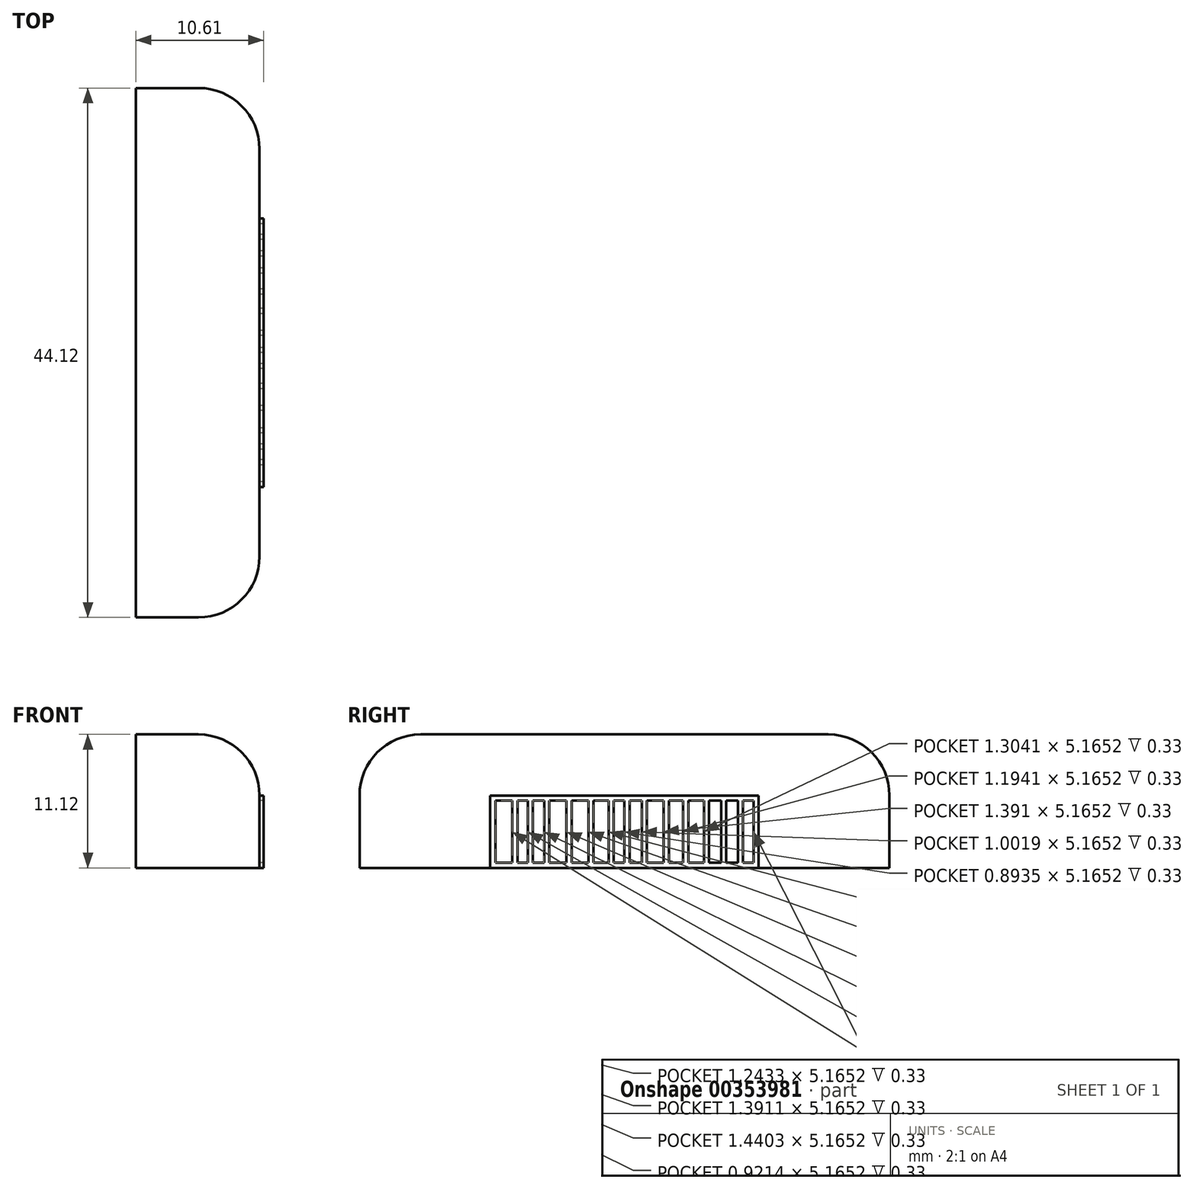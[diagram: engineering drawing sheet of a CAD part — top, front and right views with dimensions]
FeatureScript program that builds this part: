
annotation { "Feature Type Name" : "Feature", "Feature Type Description" : "" }
export const myFeature = defineFeature(function(context is Context, id is Id, definition is map)
    precondition{}
    {
        {
            var Q0;
            Q0=qCreatedBy(makeId("Right.planeOp"),FACE);
            var sketch = newSketch(context, id + "F0", { "sketchPlane" : qUnion([Q0])});
            skPoint(sketch, "E0.middle", {"position": v(0, 0) * mm});
            skLineSegment(sketch, "E1.bottom", {"start": v(22.06, -5.56) * mm, "end": v(-22.06, -5.56) * mm});
            skLineSegment(sketch, "E1.top", {"start": v(22.06, 5.56) * mm, "end": v(-22.06, 5.56) * mm});
            skLineSegment(sketch, "E1.left", {"start": v(22.06, -5.56) * mm, "end": v(22.06, 5.56) * mm});
            skLineSegment(sketch, "E1.right", {"start": v(-22.06, -5.56) * mm, "end": v(-22.06, 5.56) * mm});
            skSolve(sketch);
        }
        {
            var Q0;
            {var subQ0=sQuery(id+"F0.wireOp",EDGE,"QhqdrkBK-WLEr-STOJ-mHX4-kAFYpGoHdUyc");Q0=makeQuery(id+"F0.imprint","IMPRINT",FACE,{"disambiguationData":[TD([[makeQuery(id+"F0.imprint","IMPRINT",EDGE,{"derivedFrom":subQ0}),-1.0]])]});}
            var Q1;
            {var subQ0=sQuery(id+"F0.wireOp",EDGE,"E1.left");Q1=makeQuery(id+"F0.imprint","IMPRINT",FACE,{"disambiguationData":[TD([[makeQuery(id+"F0.imprint","IMPRINT",EDGE,{"derivedFrom":subQ0}),1.0]])]});}
            var Q2;
            {var subQ0=sQuery(id+"F0.wireOp",EDGE,"KxqXMrYp-0MTx-9sh7-7Cav-ISwPpvUKqUXm");Q2=makeQuery(id+"F0.imprint","IMPRINT",FACE,{"disambiguationData":[TD([[makeQuery(id+"F0.imprint","IMPRINT",EDGE,{"derivedFrom":subQ0}),-1.0]])]});}
            var Q3;
            {var subQ0=sQuery(id+"F0.wireOp",EDGE,"E1.right");Q3=makeQuery(id+"F0.imprint","IMPRINT",FACE,{"disambiguationData":[TD([[makeQuery(id+"F0.imprint","IMPRINT",EDGE,{"derivedFrom":subQ0}),-1.0]])]});}
            var Q4;
            {var subQ0=sQuery(id+"F0.wireOp",EDGE,"ox9cvODF-zMUq-gVxx-R5c6-Xg9GAgzpbPEs.left");Q4=makeQuery(id+"F0.imprint","IMPRINT",FACE,{"disambiguationData":[TD([[makeQuery(id+"F0.imprint","IMPRINT",EDGE,{"derivedFrom":subQ0}),1.0]])]});}
            var Q5;
            {var subQ0=sQuery(id+"F0.wireOp",EDGE,"E5YEkzb1-qd7j-ADr4-wAvl-YFfucIowREs1");Q5=makeQuery(id+"F0.imprint","IMPRINT",FACE,{"disambiguationData":[TD([[makeQuery(id+"F0.imprint","IMPRINT",EDGE,{"derivedFrom":subQ0}),-1.0]])]});}
            var Q6;
            {var subQ0=sQuery(id+"F0.wireOp",EDGE,"7jatnHy1-lAWK-yFio-aBgb-gTgx4ws20swl");Q6=makeQuery(id+"F0.imprint","IMPRINT",FACE,{"disambiguationData":[TD([[makeQuery(id+"F0.imprint","IMPRINT",EDGE,{"derivedFrom":subQ0}),1.0]])]});}
            var Q7;
            {var subQ0=sQuery(id+"F0.wireOp",EDGE,"5BvGlgIY-R3Sq-EqC4-0kwV-YxnTdAeXIUOZ");Q7=makeQuery(id+"F0.imprint","IMPRINT",FACE,{"disambiguationData":[TD([[makeQuery(id+"F0.imprint","IMPRINT",EDGE,{"derivedFrom":subQ0}),1.0]])]});}
            var Q8;
            {var subQ0=sQuery(id+"F0.wireOp",EDGE,"ox9cvODF-zMUq-gVxx-R5c6-Xg9GAgzpbPEs.right");Q8=makeQuery(id+"F0.imprint","IMPRINT",FACE,{"disambiguationData":[TD([[makeQuery(id+"F0.imprint","IMPRINT",EDGE,{"derivedFrom":subQ0}),-1.0]])]});}
            var Q9;
            {var subQ0=sQuery(id+"F0.wireOp",EDGE,"a5BHEEzq-IyKY-KC0P-sr2h-TXtUwZTsSAfV");Q9=makeQuery(id+"F0.imprint","IMPRINT",FACE,{"disambiguationData":[TD([[makeQuery(id+"F0.imprint","IMPRINT",EDGE,{"derivedFrom":subQ0}),1.0]])]});}
            var Q10;
            {var subQ0=sQuery(id+"F0.wireOp",EDGE,"bVTurAre-xmbO-HN2j-k0kJ-VzDN6Xv9tE0l");Q10=makeQuery(id+"F0.imprint","IMPRINT",FACE,{"disambiguationData":[TD([[makeQuery(id+"F0.imprint","IMPRINT",EDGE,{"derivedFrom":subQ0}),1.0]])]});}
            var Q11;
            {var subQ0=sQuery(id+"F0.wireOp",EDGE,"8v8lMbt2-ct1U-efL5-hqXj-f8Gs2E29IiBH");Q11=makeQuery(id+"F0.imprint","IMPRINT",FACE,{"disambiguationData":[TD([[makeQuery(id+"F0.imprint","IMPRINT",EDGE,{"derivedFrom":subQ0}),1.0]])]});}
            var Q12;
            {var subQ0=sQuery(id+"F0.wireOp",EDGE,"JvaCiwvk-U77r-NFcJ-Rx3I-SeJYftzx37q4");Q12=makeQuery(id+"F0.imprint","IMPRINT",FACE,{"disambiguationData":[TD([[makeQuery(id+"F0.imprint","IMPRINT",EDGE,{"derivedFrom":subQ0}),-1.0]])]});}
            extrude(context, id + "F1", {"entities" : qUnion([Q0, Q1, Q2, Q3, Q4, Q5, Q6, Q7, Q8, Q9, Q10, Q11, Q12]), "endBound" : BoundingType.SYMMETRIC, "depth" : 10.28 * mm});
        }
        {
            var Q0;
            Q0=makeQuery(id+"F1.opExtrude","CAP_EDGE",EDGE,{"disambiguationData":[OSD([sQuery(id+"F0.wireOp",EDGE,"E1.left")])],"isStart":false});
            var Q1;
            Q1=makeQuery(id+"F1.opExtrude","CAP_EDGE",EDGE,{"disambiguationData":[OSD([sQuery(id+"F0.wireOp",EDGE,"E1.right")])],"isStart":false});
            fillet(context, id + "F2", {"entities" : qUnion([Q0, Q1]), "radius" : 5.08 * mm, "tangentPropagation" : true, "allowEdgeOverflow" : false});
        }
        {
            var Q0;
            Q0=makeQuery(id+"F1.opExtrude","SWEPT_EDGE",EDGE,{"disambiguationData":[OSD([sQuery(id+"F0.wireOp",EDGE,"E1.top"),sQuery(id+"F0.wireOp",EDGE,"E1.left")])]});
            fillet(context, id + "F3", {"entities" : qUnion([Q0]), "radius" : 5.08 * mm, "tangentPropagation" : true, "allowEdgeOverflow" : false});
        }
        {
            var Q0;
            Q0=makeQuery(id+"F1.opExtrude","CAP_FACE",FACE,{"disambiguationData":[OSD([sQuery(id+"F0.wireOp",EDGE,"E1.bottom"),sQuery(id+"F0.wireOp",EDGE,"E1.top"),sQuery(id+"F0.wireOp",EDGE,"E1.left"),sQuery(id+"F0.wireOp",EDGE,"E1.right")])],"isStart":false});
            var sketch = newSketch(context, id + "F4", { "sketchPlane" : qUnion([Q0])});
            skLineSegment(sketch, "E2.bottom", {"start": v(11.18, -5.56) * mm, "end": v(-11.18, -5.56) * mm});
            skLineSegment(sketch, "E2.top", {"start": v(11.18, 0.47) * mm, "end": v(-11.18, 0.47) * mm});
            skLineSegment(sketch, "E2.left", {"start": v(11.18, -5.56) * mm, "end": v(11.18, 0.47) * mm});
            skLineSegment(sketch, "E2.right", {"start": v(-11.18, -5.56) * mm, "end": v(-11.18, 0.47) * mm});
            skPoint(sketch, "E2.middle", {"position": v(0, -2.54) * mm});
            skLineSegment(sketch, "E3", {"start": v(-8.91, 0.04) * mm, "end": v(-8.91, -5.13) * mm});
            skLineSegment(sketch, "E4", {"start": v(-8.91, -5.56) * mm, "end": v(-6.7, -5.56) * mm});
            skLineSegment(sketch, "E5", {"start": v(-6.7, -5.13) * mm, "end": v(-6.7, 0.04) * mm});
            skLineSegment(sketch, "E6", {"start": v(-6.7, 0.47) * mm, "end": v(-4.82, 0.47) * mm});
            skLineSegment(sketch, "E7", {"start": v(-4.82, 0.04) * mm, "end": v(-4.82, -5.13) * mm});
            skLineSegment(sketch, "E8", {"start": v(-4.82, -5.56) * mm, "end": v(-3, -5.56) * mm});
            skLineSegment(sketch, "E9", {"start": v(-3, -5.13) * mm, "end": v(-3, 0.04) * mm});
            skLineSegment(sketch, "E10", {"start": v(-3, 0.47) * mm, "end": v(-1.33, 0.47) * mm});
            skLineSegment(sketch, "E11", {"start": v(-1.33, 0.04) * mm, "end": v(-1.33, -5.13) * mm});
            skLineSegment(sketch, "E12", {"start": v(-1.33, -5.56) * mm, "end": v(0, -5.56) * mm});
            skLineSegment(sketch, "E13", {"start": v(0, -5.13) * mm, "end": v(0, 0.04) * mm});
            skLineSegment(sketch, "E14", {"start": v(0, 0.47) * mm, "end": v(1.43, 0.47) * mm});
            skLineSegment(sketch, "E15", {"start": v(1.43, 0.04) * mm, "end": v(1.43, -5.13) * mm});
            skLineSegment(sketch, "E16", {"start": v(1.43, -5.56) * mm, "end": v(3.26, -5.56) * mm});
            skLineSegment(sketch, "E17", {"start": v(3.26, -5.13) * mm, "end": v(3.26, 0.04) * mm});
            skLineSegment(sketch, "E18", {"start": v(3.26, 0.47) * mm, "end": v(4.88, 0.47) * mm});
            skLineSegment(sketch, "E19", {"start": v(4.88, 0.04) * mm, "end": v(4.88, -5.13) * mm});
            skLineSegment(sketch, "E20", {"start": v(4.88, -5.56) * mm, "end": v(7.05, -5.56) * mm});
            skLineSegment(sketch, "E21", {"start": v(7.05, -5.13) * mm, "end": v(7.05, 0.04) * mm});
            skLineSegment(sketch, "E22", {"start": v(7.05, 0.47) * mm, "end": v(8.48, 0.47) * mm});
            skLineSegment(sketch, "E23", {"start": v(8.48, 0.04) * mm, "end": v(8.48, -5.13) * mm});
            skLineSegment(sketch, "E24", {"start": v(8.48, -5.56) * mm, "end": v(9.44, -5.56) * mm});
            skLineSegment(sketch, "E25", {"start": v(9.44, -5.13) * mm, "end": v(9.44, 0.04) * mm});
            skLineSegment(sketch, "E26.0", {"start": v(10.75, 0.04) * mm, "end": v(9.87, 0.04) * mm});
            skLineSegment(sketch, "E27.0", {"start": v(-10.75, -5.13) * mm, "end": v(-10.75, 0.04) * mm});
            skLineSegment(sketch, "E28.0", {"start": v(10.75, -5.13) * mm, "end": v(10.75, 0.04) * mm});
            skLineSegment(sketch, "E29.0", {"start": v(10.75, -5.13) * mm, "end": v(9.87, -5.13) * mm});
            skLineSegment(sketch, "E30.0", {"start": v(-9.34, 0.04) * mm, "end": v(-9.34, -5.13) * mm});
            skLineSegment(sketch, "E31.0", {"start": v(-6.26, -5.13) * mm, "end": v(-6.26, 0.04) * mm});
            skLineSegment(sketch, "E32.0", {"start": v(-4.4, 0.04) * mm, "end": v(-4.4, -5.13) * mm});
            skLineSegment(sketch, "E33.0", {"start": v(-2.57, -5.13) * mm, "end": v(-2.57, 0.04) * mm});
            skLineSegment(sketch, "E34.0", {"start": v(-0.9, 0.04) * mm, "end": v(-0.9, -5.13) * mm});
            skLineSegment(sketch, "E35.0", {"start": v(0.43, -5.13) * mm, "end": v(0.43, 0.04) * mm});
            skLineSegment(sketch, "E36.0", {"start": v(1.87, 0.04) * mm, "end": v(1.87, -5.13) * mm});
            skLineSegment(sketch, "E37.0", {"start": v(3.69, -5.13) * mm, "end": v(3.69, 0.04) * mm});
            skLineSegment(sketch, "E38.0", {"start": v(5.31, 0.04) * mm, "end": v(5.31, -5.13) * mm});
            skLineSegment(sketch, "E39.0", {"start": v(6.62, -5.13) * mm, "end": v(6.62, 0.04) * mm});
            skLineSegment(sketch, "E40.0", {"start": v(8.05, 0.04) * mm, "end": v(8.05, -5.13) * mm});
            skLineSegment(sketch, "E41.0", {"start": v(9.87, -5.13) * mm, "end": v(9.87, 0.04) * mm});
            skLineSegment(sketch, "E42", {"start": v(-8.05, 0.04) * mm, "end": v(-8.05, -5.13) * mm});
            skLineSegment(sketch, "E43.0", {"start": v(-7.62, 0.04) * mm, "end": v(-7.62, -5.13) * mm});
            skLineSegment(sketch, "E44.trimOffspring", {"start": v(0, -5.13) * mm, "end": v(-0.9, -5.13) * mm});
            skLineSegment(sketch, "E45.trimOffspring", {"start": v(1.43, -5.13) * mm, "end": v(0.43, -5.13) * mm});
            skLineSegment(sketch, "E46.trimOffspring", {"start": v(-1.33, -5.13) * mm, "end": v(-2.57, -5.13) * mm});
            skLineSegment(sketch, "E47.trimOffspring", {"start": v(-3, -5.13) * mm, "end": v(-4.4, -5.13) * mm});
            skLineSegment(sketch, "E48.trimOffspring", {"start": v(3.26, -5.13) * mm, "end": v(1.87, -5.13) * mm});
            skLineSegment(sketch, "E49.trimOffspring", {"start": v(4.88, -5.13) * mm, "end": v(3.69, -5.13) * mm});
            skLineSegment(sketch, "E50.trimOffspring", {"start": v(6.62, -5.13) * mm, "end": v(5.31, -5.13) * mm});
            skLineSegment(sketch, "E51.trimOffspring", {"start": v(8.05, -5.13) * mm, "end": v(7.05, -5.13) * mm});
            skLineSegment(sketch, "E52.trimOffspring", {"start": v(9.44, -5.13) * mm, "end": v(8.48, -5.13) * mm});
            skLineSegment(sketch, "E53.trimOffspring", {"start": v(-4.82, -5.13) * mm, "end": v(-6.26, -5.13) * mm});
            skLineSegment(sketch, "E54.trimOffspring", {"start": v(-6.7, -5.13) * mm, "end": v(-7.62, -5.13) * mm});
            skLineSegment(sketch, "E55.trimOffspring", {"start": v(-8.05, -5.13) * mm, "end": v(-8.91, -5.13) * mm});
            skLineSegment(sketch, "E56.trimOffspring", {"start": v(-9.34, -5.13) * mm, "end": v(-10.75, -5.13) * mm});
            skLineSegment(sketch, "E57.trimOffspring", {"start": v(-9.34, 0.04) * mm, "end": v(-10.75, 0.04) * mm});
            skLineSegment(sketch, "E58.trimOffspring", {"start": v(-8.05, 0.04) * mm, "end": v(-8.91, 0.04) * mm});
            skLineSegment(sketch, "E59.trimOffspring", {"start": v(-6.7, 0.04) * mm, "end": v(-7.62, 0.04) * mm});
            skLineSegment(sketch, "E60.trimOffspring", {"start": v(-4.82, 0.04) * mm, "end": v(-6.26, 0.04) * mm});
            skLineSegment(sketch, "E61.trimOffspring", {"start": v(-3, 0.04) * mm, "end": v(-4.4, 0.04) * mm});
            skLineSegment(sketch, "E62.trimOffspring", {"start": v(-1.33, 0.04) * mm, "end": v(-2.57, 0.04) * mm});
            skLineSegment(sketch, "E63.trimOffspring", {"start": v(0, 0.04) * mm, "end": v(-0.9, 0.04) * mm});
            skLineSegment(sketch, "E64.trimOffspring", {"start": v(1.43, 0.04) * mm, "end": v(0.43, 0.04) * mm});
            skLineSegment(sketch, "E65.trimOffspring", {"start": v(3.26, 0.04) * mm, "end": v(1.87, 0.04) * mm});
            skLineSegment(sketch, "E66.trimOffspring", {"start": v(4.88, 0.04) * mm, "end": v(3.69, 0.04) * mm});
            skLineSegment(sketch, "E67.trimOffspring", {"start": v(6.62, 0.04) * mm, "end": v(5.31, 0.04) * mm});
            skLineSegment(sketch, "E68.trimOffspring", {"start": v(8.05, 0.04) * mm, "end": v(7.05, 0.04) * mm});
            skLineSegment(sketch, "E69.trimOffspring", {"start": v(9.44, 0.04) * mm, "end": v(8.48, 0.04) * mm});
            skSolve(sketch);
        }
        {
            var Q0;
            Q0 = qSketchRegion(id + "F4", true);
            extrude(context, id + "F5", {"entities" : qUnion([Q0]), "operationType" : NewBodyOperationType.ADD, "depth" : 0.33 * mm});
        }
    });
